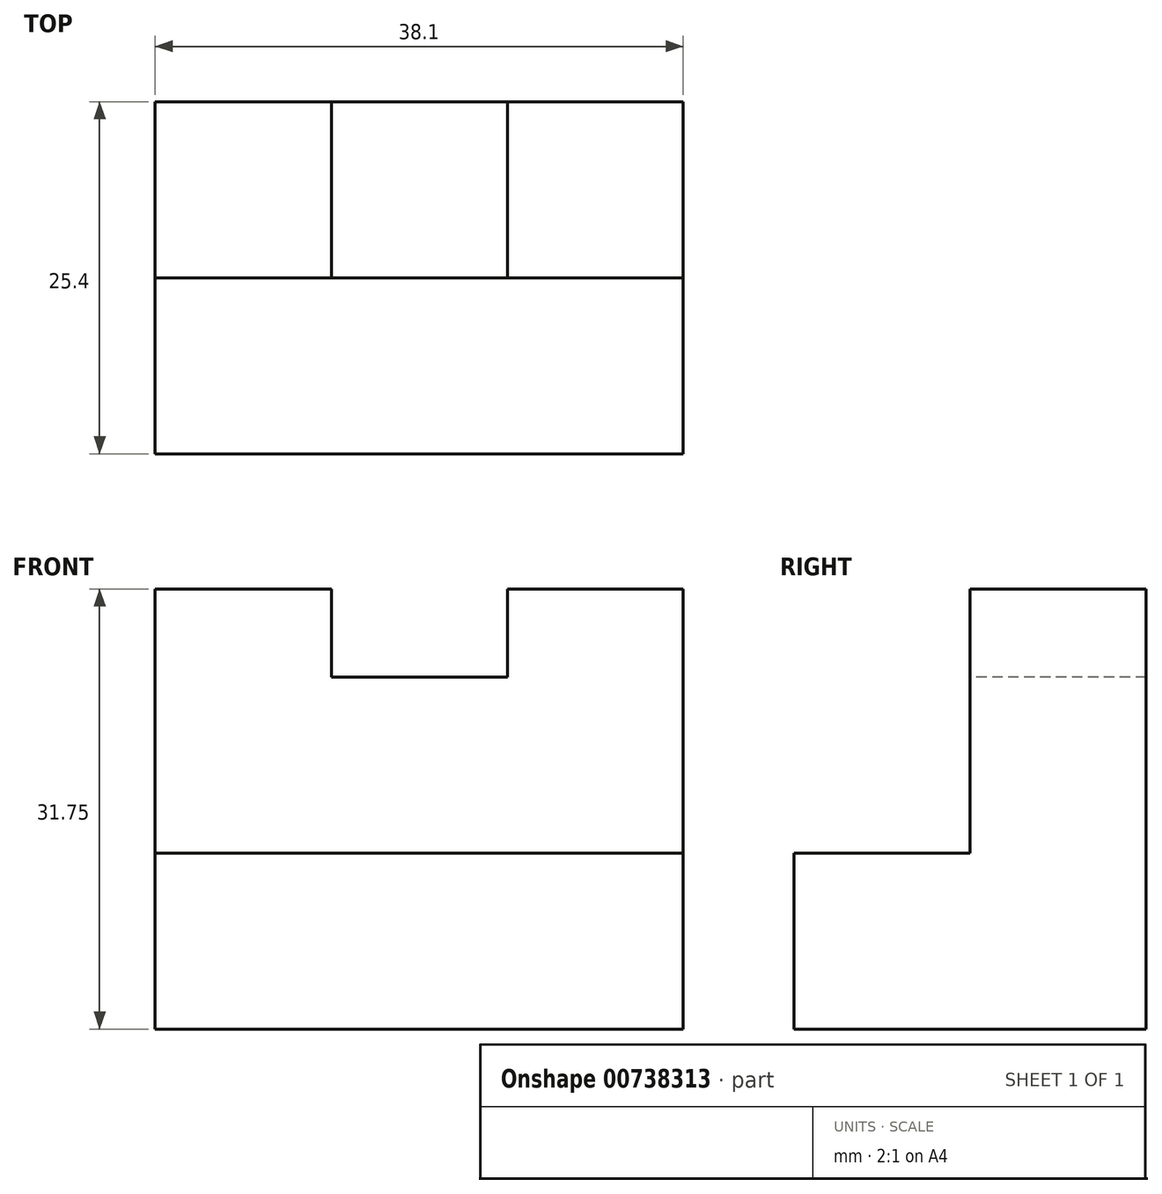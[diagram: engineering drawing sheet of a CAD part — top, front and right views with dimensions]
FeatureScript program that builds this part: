
annotation { "Feature Type Name" : "Feature", "Feature Type Description" : "" }
export const myFeature = defineFeature(function(context is Context, id is Id, definition is map)
    precondition{}
    {
        {
            var Q0;
            Q0=qCreatedBy(makeId("Right.planeOp"),FACE);
            var sketch = newSketch(context, id + "F0", { "sketchPlane" : qUnion([Q0])});
            skLineSegment(sketch, "E0", {"start": v(0, 0) * mm, "end": v(0, 31.75) * mm});
            skLineSegment(sketch, "E1", {"start": v(0, 31.75) * mm, "end": v(-12.7, 31.75) * mm});
            skLineSegment(sketch, "E2", {"start": v(-12.7, 31.75) * mm, "end": v(-12.7, 12.7) * mm});
            skLineSegment(sketch, "E3", {"start": v(-12.7, 12.7) * mm, "end": v(-25.4, 12.7) * mm});
            skLineSegment(sketch, "E4", {"start": v(-25.4, 12.7) * mm, "end": v(-25.4, 0) * mm});
            skLineSegment(sketch, "E5", {"start": v(-25.4, 0) * mm, "end": v(0, 0) * mm});
            skSolve(sketch);
        }
        {
            var Q0;
            Q0=makeQuery(id+"F0.imprint","IMPRINT",FACE,{"disambiguationData":[TD([[makeQuery(id+"F0.imprint","IMPRINT",EDGE,{"derivedFrom":sQuery(id+"F0.wireOp",EDGE,"E0")}),1.0]])]});
            extrude(context, id + "F1", {"entities" : qUnion([Q0]), "depth" : 38.1 * mm, "offsetDistance" : 25.4 * mm});
        }
        {
            var Q0;
            Q0=makeQuery(id+"F1.opExtrude","SWEPT_FACE",FACE,{"disambiguationData":[OSD([sQuery(id+"F0.wireOp",EDGE,"E2")])]});
            var sketch = newSketch(context, id + "F2", { "sketchPlane" : qUnion([Q0])});
            skLineSegment(sketch, "E6", {"start": v(12.73, 31.75) * mm, "end": v(12.73, 25.4) * mm});
            skLineSegment(sketch, "E7", {"start": v(12.73, 25.4) * mm, "end": v(25.43, 25.4) * mm});
            skLineSegment(sketch, "E8", {"start": v(25.43, 25.4) * mm, "end": v(25.43, 31.75) * mm});
            skLineSegment(sketch, "E9", {"start": v(25.43, 31.75) * mm, "end": v(38.1, 31.75) * mm});
            skLineSegment(sketch, "E10", {"start": v(38.1, 31.75) * mm, "end": v(25.43, 31.75) * mm});
            skSolve(sketch);
        }
        {
            var Q0;
            {var subQ0=sQuery(id+"F2.wireOp",EDGE,"E6");Q0=makeQuery(id+"F2.imprint","IMPRINT",FACE,{"disambiguationData":[TD([[makeQuery(id+"F2.imprint","IMPRINT",EDGE,{"derivedFrom":subQ0}),1.0]])]});}
            extrude(context, id + "F3", {"entities" : qUnion([Q0]), "operationType" : NewBodyOperationType.REMOVE, "endBound" : BoundingType.THROUGH_ALL, "oppositeDirection" : true, "depth" : 25.4 * mm, "offsetDistance" : 25.4 * mm});
        }
    });
